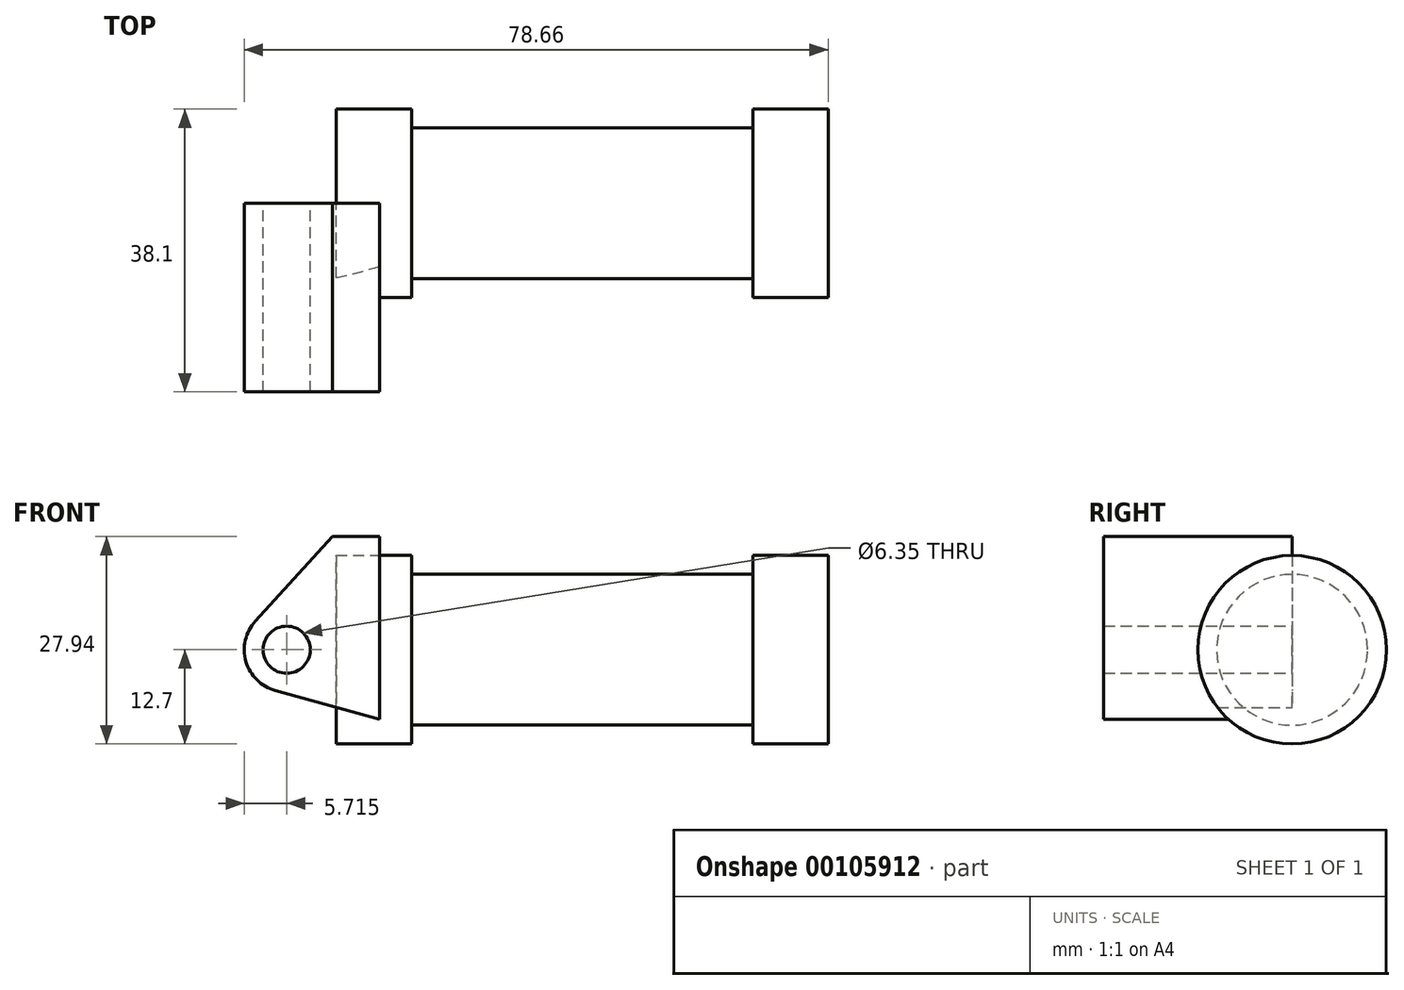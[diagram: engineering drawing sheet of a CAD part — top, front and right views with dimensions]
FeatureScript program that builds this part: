
annotation { "Feature Type Name" : "Feature", "Feature Type Description" : "" }
export const myFeature = defineFeature(function(context is Context, id is Id, definition is map)
    precondition{}
    {
        {
            var Q0;
            Q0=qCreatedBy(makeId("Front.planeOp"),FACE);
            var sketch = newSketch(context, id + "F0", { "sketchPlane" : qUnion([Q0])});
            skLineSegment(sketch, "E0", {"start": v(0, 0) * mm, "end": v(0, 12.7) * mm});
            skLineSegment(sketch, "E1", {"start": v(0, 12.7) * mm, "end": v(10.16, 12.7) * mm});
            skLineSegment(sketch, "E2", {"start": v(10.16, 12.7) * mm, "end": v(10.16, 10.16) * mm});
            skLineSegment(sketch, "E3", {"start": v(10.16, 10.16) * mm, "end": v(56.13, 10.16) * mm});
            skLineSegment(sketch, "E4", {"start": v(56.13, 10.16) * mm, "end": v(56.13, 12.7) * mm});
            skLineSegment(sketch, "E5", {"start": v(56.13, 12.7) * mm, "end": v(66.3, 12.7) * mm});
            skLineSegment(sketch, "E6", {"start": v(66.3, 12.7) * mm, "end": v(66.3, 0) * mm});
            skLineSegment(sketch, "E7", {"start": v(66.3, 0) * mm, "end": v(0, 0) * mm});
            skLineSegment(sketch, "E8", {"start": v(5.84, 15.24) * mm, "end": v(-0.5, 15.24) * mm});
            skLineSegment(sketch, "E9", {"start": v(-0.5, 15.24) * mm, "end": v(-10.88, 3.85) * mm});
            skLineSegment(sketch, "E10", {"start": v(0, 0) * mm, "end": v(-6.65, 0) * mm});
            skCircle(sketch, "E11", {"center": v(-6.65, 0) * mm, "radius": 5.72 * mm});
            skCircle(sketch, "E12", {"center": v(-6.65, 0) * mm, "radius": 3.18 * mm});
            skLineSegment(sketch, "E13", {"start": v(5.84, 15.24) * mm, "end": v(5.84, -9.4) * mm});
            skLineSegment(sketch, "E14", {"start": v(5.84, -9.4) * mm, "end": v(-8.18, -5.5) * mm});
            skSolve(sketch);
        }
        {
            var Q0;
            {var subQ0=sQuery(id+"F0.wireOp",EDGE,"E0");Q0=makeQuery(id+"F0.imprint","IMPRINT",FACE,{"disambiguationData":[TD([[makeQuery(id+"F0.imprint","IMPRINT",EDGE,{"derivedFrom":subQ0}),-1.0]])]});}
            var Q1;
            {var subQ0=sQuery(id+"F0.wireOp",EDGE,"E2");Q1=makeQuery(id+"F0.imprint","IMPRINT",FACE,{"disambiguationData":[TD([[makeQuery(id+"F0.imprint","IMPRINT",EDGE,{"derivedFrom":subQ0}),-1.0]])]});}
            var Q2;
            Q2=sQuery(id+"F0.wireOp",EDGE,"E7");
            revolve(context, id + "F1", {"entities" : qUnion([Q0, Q1]), "axis" : qUnion([Q2]), "revolveType" : RevolveType.FULL});
        }
        {
            var Q0;
            {var subQ3=sQuery(id+"F0.wireOp",EDGE,"E0");Q0=makeQuery(id+"F0.imprint","IMPRINT",FACE,{"disambiguationData":[TD([[makeQuery(id+"F0.imprint","IMPRINT",EDGE,{"derivedFrom":subQ3}),1.0]])]});}
            var Q1;
            {var subQ4=sQuery(id+"F0.wireOp",EDGE,"E12");Q1=makeQuery(id+"F0.imprint","IMPRINT",FACE,{"disambiguationData":[TD([[makeQuery(id+"F0.imprint","IMPRINT",EDGE,{"derivedFrom":subQ4}),-1.0]])]});}
            var Q2;
            {var subQ0=sQuery(id+"F0.wireOp",EDGE,"E14");Q2=makeQuery(id+"F0.imprint","IMPRINT",FACE,{"disambiguationData":[TD([[makeQuery(id+"F0.imprint","IMPRINT",EDGE,{"derivedFrom":subQ0}),-1.0]])]});}
            var Q3;
            {var subQ0=sQuery(id+"F0.wireOp",EDGE,"E0");Q3=makeQuery(id+"F0.imprint","IMPRINT",FACE,{"disambiguationData":[TD([[makeQuery(id+"F0.imprint","IMPRINT",EDGE,{"derivedFrom":subQ0}),-1.0]])]});}
            extrude(context, id + "F2", {"entities" : qUnion([Q0, Q1, Q2, Q3]), "operationType" : NewBodyOperationType.ADD, "depth" : 25.4 * mm});
        }
    });
